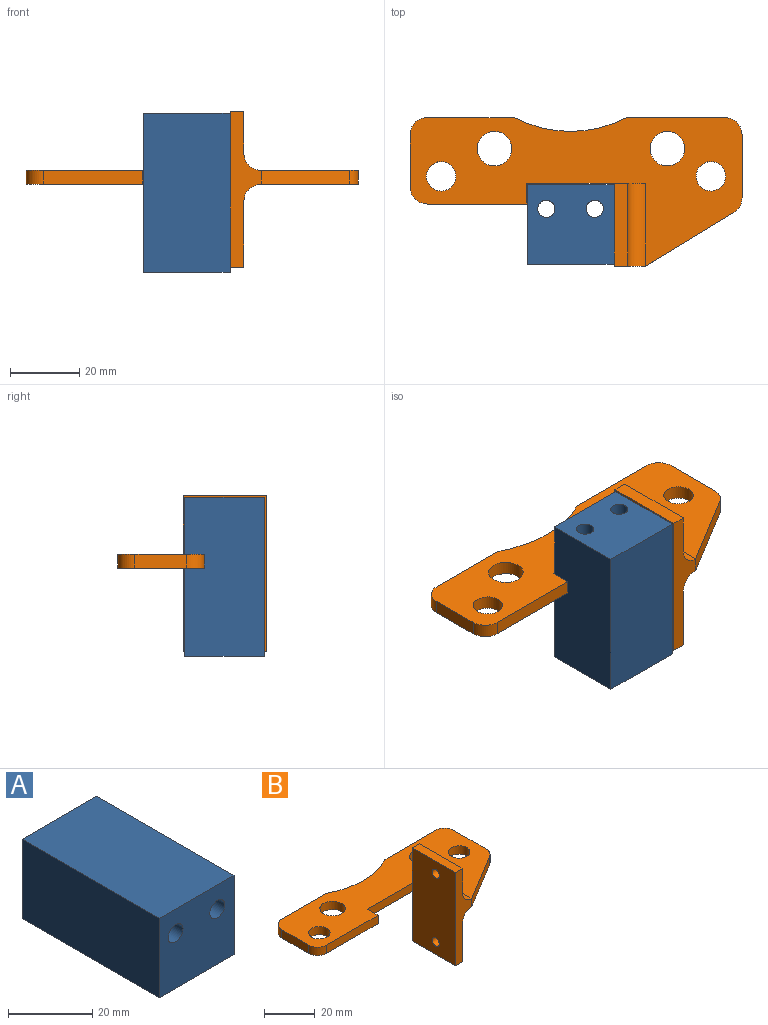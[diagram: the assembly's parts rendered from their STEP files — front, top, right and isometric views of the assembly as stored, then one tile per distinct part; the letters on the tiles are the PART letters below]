
ASSEMBLY  parts=2 mates=1
PART A: 8 faces, bbox 25x46x23 mm
  f0: plane 46x25mm, normal (0,0,1), area 1150mm2, adj f1,f5,f6,f7
  f1: plane 46x23mm, normal (-1,0,0), area 1058mm2, adj f0,f2,f6,f7
  f2: plane 46x25mm, normal (0,0,-1), area 1150mm2, adj f1,f5,f6,f7
  f3: cylinder r=2.5mm len=46mm, axis (0,1,0), area 722.6mm2, adj f6,f7
  f4: cylinder r=2.5mm len=46mm, axis (0,1,0), area 722.6mm2, adj f6,f7
  f5: plane 46x23mm, normal (1,0,0), area 1058mm2, adj f0,f2,f6,f7
  f6: plane 25x23mm, normal (0,-1,0), area 535.7mm2, adj f0,f1,f2,f3,f4,f5
  f7: plane 25x23mm, normal (0,1,0), area 535.7mm2, adj f0,f1,f2,f3,f4,f5
PART B: 31 faces, bbox 96x43x45 mm
  f0: plane 96x43mm, normal (0,0,-1), area 2085.2mm2, adj f1,f2,f6,f9,f12,f13,f14,f15
  f1: plane 18.19x4mm, normal (1,0,0), area 72.7mm2, adj f0,f3,f27,f30
  f2: plane 28.35x4mm, normal (0,1,0), area 113.4mm2, adj f0,f3,f21,f27
  f3: plane 96x43mm, normal (0,0,1), area 2085.2mm2, adj f1,f2,f6,f9,f12,f13,f14,f15
  f4: plane 45x24mm, normal (-1,0,0), area 1054.9mm2, adj f7,f8,f10,f13,f19,f20,f22,f23
  f5: plane 24x12mm, normal (1,0,0), area 275.4mm2, adj f7,f8,f19,f23,f25
  f6: plane 25.15x4mm, normal (0,1,0), area 100.6mm2, adj f0,f3,f21,f28
  f7: plane 45x9mm, normal (0,-1,0), area 210.7mm2, adj f4,f5,f8,f10,f11,f24,f25,f29
  f8: plane 24x4mm, normal (0,0,1), area 96mm2, adj f4,f5,f7,f19
  f9: plane 15x4mm, normal (-1,0,0), area 60mm2, adj f0,f3,f26,f28
  f10: plane 24x4mm, normal (0,0,-1), area 96mm2, adj f4,f7,f11,f20
  f11: plane 24x19mm, normal (1,0,0), area 443.4mm2, adj f7,f10,f20,f22,f24
  f12: plane 28.8x4mm, normal (0,-1,0), area 115.2mm2, adj f0,f3,f14,f26
  f13: plane 25.2x4mm, normal (0,-1,0), area 100.8mm2, adj f0,f3,f4,f14
  f14: plane 6x4mm, normal (1,0,0), area 24mm2, adj f0,f3,f12,f13
  f15: cylinder r=4.25mm len=8.5mm, axis (0,0,-1), area 106.8mm2, adj f0,f3
  f16: cylinder r=5mm len=10mm, axis (0,0,-1), area 125.7mm2, adj f0,f3
  f17: cylinder r=5mm len=10mm, axis (0,0,-1), area 125.7mm2, adj f0,f3
  f18: cylinder r=4.25mm len=8.5mm, axis (0,0,-1), area 106.8mm2, adj f0,f3
  f19: plane 17x9mm, normal (0,1,0), area 73.4mm2, adj f3,f4,f5,f8,f25
  f20: plane 24x9mm, normal (0,1,0), area 101.4mm2, adj f0,f4,f10,f11,f24
  f21: cylinder r=35mm len=32.5mm, axis (0,0,-1), area 135.2mm2, adj f0,f2,f3,f6
  f22: cylinder r=2mm len=4mm, axis (-1,0,0), area 50.3mm2, adj f4,f11
  f23: cylinder r=2mm len=4mm, axis (-1,0,0), area 50.3mm2, adj f4,f5
  f24: cylinder r=5mm len=24mm, axis (0,1,0), area 188.5mm2, adj f0,f7,f11,f20
  f25: cylinder r=5mm len=24mm, axis (0,-1,0), area 188.5mm2, adj f3,f5,f7,f19
  f26: cylinder r=5mm len=5mm, axis (0,0,1), area 31.4mm2, adj f0,f3,f9,f12
  f27: cylinder r=5mm len=5mm, axis (0,0,1), area 31.4mm2, adj f0,f1,f2,f3
  f28: cylinder r=5mm len=5mm, axis (0,0,-1), area 31.4mm2, adj f0,f3,f6,f9
  f29: plane 25.6x15.54mm, normal (0.52,-0.85,0), area 119.8mm2, adj f0,f3,f7,f30
  f30: cylinder r=5mm len=4.27mm, axis (0,0,-1), area 20.5mm2, adj f0,f1,f3,f29
PLACE A rot(axis=(-1,0,0),90deg) t=(-23.9,-19.46,-18.68)mm
PLACE B t=(25.6,11.44,6.81)mm fixed
MATE parallel A.f5 <-> B.f4  axis (-1,0,0) through (-11.4,-19.46,4.32)mm
